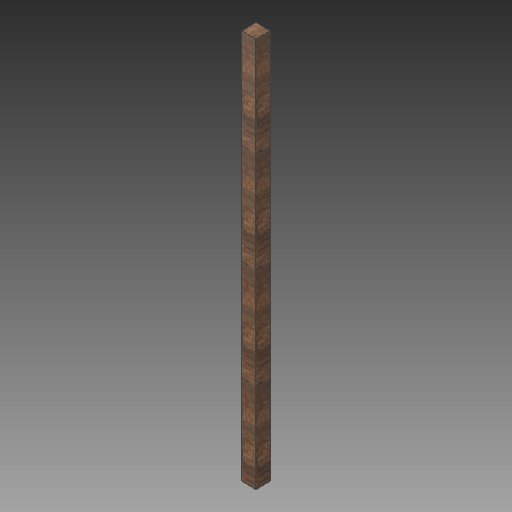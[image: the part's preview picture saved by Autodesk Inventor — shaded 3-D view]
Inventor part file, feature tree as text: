
AUTODESK INVENTOR PART (.ipt)
format: ipt  version: 2017 (Build 210142000, 142)  size: 104,448 bytes
history: native  units: in
note: dims shown in document units (in); Inventor stores cm internally (conversion verified against a paired STEP export)
features: extrude x1, sketch x1
ambient origin geometry x8: Origin, YZ Plane, XZ Plane, XY Plane, X Axis, Y Axis, Z Axis, Center Point
bodies: Solid1 (feature_tree)
feature tree (2):
  extrude  "Extrusion1"  Depth=3.5in
  sketch  "Sketch1"  dims[d0=3.5in d1=3.5in d2=96.0in d3=0.0in]
